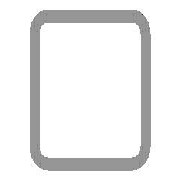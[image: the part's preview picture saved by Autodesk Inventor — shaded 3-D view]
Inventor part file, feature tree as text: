
AUTODESK INVENTOR PART (.ipt)
format: ipt  version: 2025 (Build 290162010, 162A)  size: 132,608 bytes
history: native  units: mm (DEFAULTED — no unit token found)
features: other x4, sketch x1, plane x1
ambient origin geometry x8: Origin, YZ Plane, XZ Plane, XY Plane, X Axis, Y Axis, Z Axis, Center Point
bodies: Solid1 (feature_tree), Body (feature_tree)
feature tree (6):
  parser-record x1  (decoder bookkeeping rows leaked as tree rows — omitted from the tree; the rows remain in map.json)
  other  "Driven Length"
  other  "Start Plane"
  other  "End Plane"
  sketch  "Sketch3"  dims[d3=2350.0mm d4=0.0mm d7=6.0mm d9=50.0mm d11=50.0mm d12=3.0mm d13=-0.0mm d14=2350.0mm d15=25.0mm d16=25.0mm d17=90.0deg d18=2350.0mm]
  plane  "Work Plane3"
